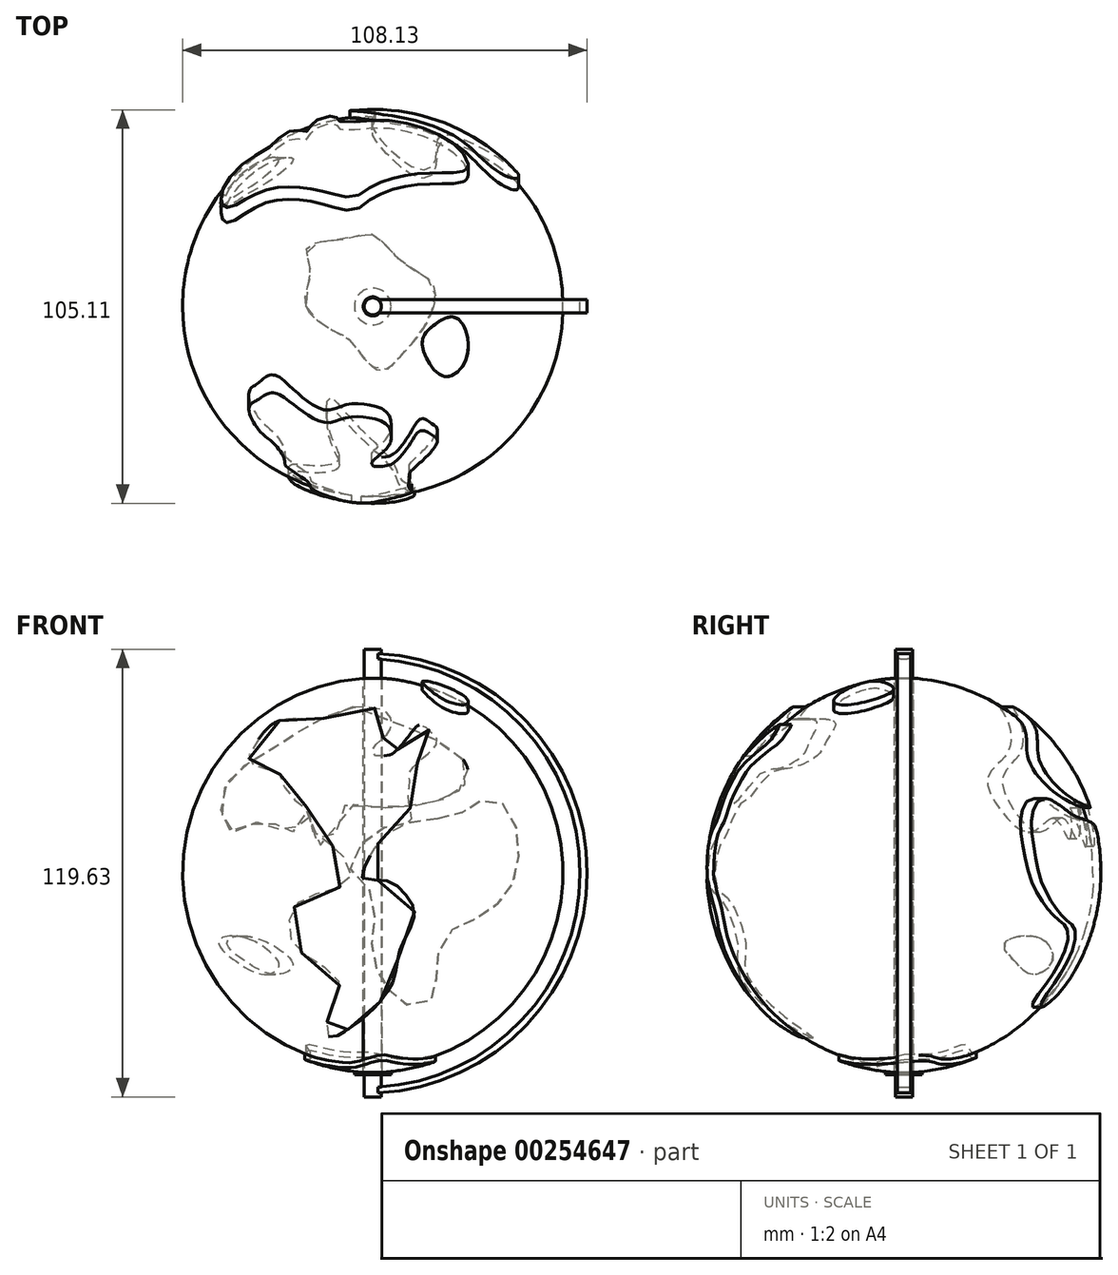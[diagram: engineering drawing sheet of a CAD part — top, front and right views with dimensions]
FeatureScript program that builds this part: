
annotation { "Feature Type Name" : "Feature", "Feature Type Description" : "" }
export const myFeature = defineFeature(function(context is Context, id is Id, definition is map)
    precondition{}
    {
        {
            var Q0;
            Q0=qCreatedBy(makeId("Front.planeOp"),FACE);
            var sketch = newSketch(context, id + "F0", { "sketchPlane" : qUnion([Q0])});
            skLineSegment(sketch, "E0", {"start": v(0, 76.2) * mm, "end": v(0, -76.2) * mm, "construction": true});
            skLineSegment(sketch, "E1", {"start": v(-76.2, 0) * mm, "end": v(76.2, 0) * mm, "construction": true});
            skLineSegment(sketch, "E2", {"start": v(0, 0) * mm, "end": v(0, 50.8) * mm});
            skLineSegment(sketch, "E3", {"start": v(0, 0) * mm, "end": v(0, -53.5) * mm});
            skLineSegment(sketch, "E4", {"start": v(0, 0) * mm, "end": v(50.8, 0) * mm});
            skArc(sketch, "E5", {"start": v(0, -53.5) * mm, "mid": v(50.82, -1.35) * mm, "end": v(0, 50.8) * mm});
            skSolve(sketch);
        }
        {
            var Q0;
            Q0 = qSketchRegion(id + "F0", true);
            var Q1;
            Q1=sQuery(id+"F0.wireOp",EDGE,"E0");
            revolve(context, id + "F1", {"entities" : qUnion([Q0]), "axis" : qUnion([Q1]), "revolveType" : RevolveType.FULL});
        }
        {
            var Q0;
            Q0=qCreatedBy(makeId("Front.planeOp"),FACE);
            var sketch = newSketch(context, id + "F2", { "sketchPlane" : qUnion([Q0])});
            skFitSpline(sketch, "E6", {"points": [v(24.15, 28.93) * mm, v(0, 41.12) * mm, v(-5.65, 42.93) * mm, v(-17.84, 37.5) * mm, v(-30.04, 29.83) * mm, v(-38.16, 23.96) * mm, v(-40.42, 14.93) * mm, v(-36.8, 9.52) * mm, v(-27.33, 13.13) * mm, v(-23.71, 7.71) * mm, v(-18.75, 14.48) * mm, v(-17.84, 15.84) * mm, v(-13.78, 5.9) * mm, v(-10.17, 8.61) * mm, v(-7.91, 16.29) * mm, v(0, 16.29) * mm, v(7.44, 16.29) * mm, v(22.8, 20.35) * mm, v(24.15, 28.93) * mm]});
            skFitSpline(sketch, "E7", {"points": [v(17.37, 13.13) * mm, v(24.15, 14.93) * mm, v(31.37, 18.55) * mm, v(37.7, 12.68) * mm, v(38.6, 0) * mm, v(35.88, -6.74) * mm, v(28.66, -13.06) * mm, v(20.98, -16.67) * mm, v(17.37, -23.44) * mm, v(16.02, -34.73) * mm, v(10.15, -36.99) * mm, v(0, -23.44) * mm, v(0, -7.19) * mm, v(-6.1, 0) * mm, v(0, 9.06) * mm, v(7.44, 11.77) * mm, v(17.37, 13.13) * mm]});
            skSolve(sketch);
        }
        {
            var Q0;
            Q0 = qSketchRegion(id + "F2", true);
            extrude(context, id + "F3", {"entities" : qUnion([Q0]), "operationType" : NewBodyOperationType.ADD, "oppositeDirection" : true, "depth" : 54.36 * mm, "hasSecondDirection" : true, "secondDirectionOppositeDirection" : true, "secondDirectionDepth" : 11.18 * mm});
        }
        {
            var Q0;
            Q0=qCreatedBy(makeId("Right.planeOp"),FACE);
            var sketch = newSketch(context, id + "F4", { "sketchPlane" : qUnion([Q0])});
            skFitSpline(sketch, "E8", {"points": [v(36.7, -18.93) * mm, v(39.41, -25.7) * mm, v(34, -28.41) * mm, v(29.93, -25.25) * mm, v(26.77, -20.28) * mm, v(36.7, -18.93) * mm]});
            skSolve(sketch);
        }
        {
            var Q0;
            Q0 = qSketchRegion(id + "F4", true);
            extrude(context, id + "F5", {"entities" : qUnion([Q0]), "operationType" : NewBodyOperationType.ADD, "oppositeDirection" : true, "depth" : 56.4 * mm, "hasSecondDirection" : true, "secondDirectionOppositeDirection" : true, "secondDirectionDepth" : 6.6 * mm});
        }
        {
            var Q0;
            Q0=qCreatedBy(makeId("Front.planeOp"),FACE);
            var sketch = newSketch(context, id + "F6", { "sketchPlane" : qUnion([Q0])});
            skArc(sketch, "E9", {"start": v(0, -54.77) * mm, "mid": v(52.65, -1.08) * mm, "end": v(0, 52.61) * mm});
            skLineSegment(sketch, "E10", {"start": v(0, 52.61) * mm, "end": v(0, 70.09) * mm});
            skLineSegment(sketch, "E11", {"start": v(0, 70.09) * mm, "end": v(87.72, 70.09) * mm});
            skLineSegment(sketch, "E12", {"start": v(87.72, 70.09) * mm, "end": v(87.72, -75.77) * mm});
            skLineSegment(sketch, "E13", {"start": v(87.72, -75.77) * mm, "end": v(0, -75.77) * mm});
            skLineSegment(sketch, "E14", {"start": v(0, -75.77) * mm, "end": v(0, -54.77) * mm});
            skSolve(sketch);
        }
        {
            var Q0;
            Q0 = qSketchRegion(id + "F2", true);
            extrude(context, id + "F7", {"entities" : qUnion([Q0]), "operationType" : NewBodyOperationType.ADD, "oppositeDirection" : true, "depth" : 57.66 * mm});
        }
        {
            var Q0;
            Q0=qCreatedBy(makeId("Front.planeOp"),FACE);
            var sketch = newSketch(context, id + "F8", { "sketchPlane" : qUnion([Q0])});
            skFitSpline(sketch, "E15", {"points": [v(-24.96, 39.32) * mm, v(-30.83, 33.9) * mm, v(-33.09, 29.38) * mm, v(-30.38, 26.67) * mm, v(-26.32, 26.22) * mm, v(-23.6, 22.61) * mm, v(-23.16, 19.45) * mm, v(-17.74, 16.29) * mm, v(-16.38, 10.42) * mm, v(-14.13, 8.16) * mm, v(-11.87, 6.8) * mm, v(-6, 0) * mm, v(-6.45, -3.58) * mm, v(-12.32, -6.29) * mm, v(-20.9, -10.35) * mm, v(-21.8, -19.38) * mm, v(-17.74, -23.44) * mm, v(-14.13, -25.7) * mm, v(-9.16, -30.22) * mm, v(-9.61, -34.28) * mm, v(-11.87, -39.7) * mm, v(-11.87, -45.12) * mm, v(-9.16, -44.66) * mm, v(0, -37.9) * mm, v(5.74, -29.31) * mm, v(7.55, -21.19) * mm, v(11.16, -11.7) * mm, v(7.55, -5.83) * mm, v(4.39, -3.58) * mm, v(-2.7, -2.7) * mm, v(-2.3, 0) * mm, v(3.67, 8.81) * mm, v(10.25, 12.93) * mm, v(9.64, 17.45) * mm, v(9.84, 23) * mm, v(9.84, 25.48) * mm, v(12.52, 28.56) * mm, v(17.25, 33.5) * mm, v(16.01, 35.76) * mm, v(12.93, 38.23) * mm, v(10.66, 36.58) * mm, v(5.73, 30.82) * mm, v(3.26, 30) * mm, v(0, 30.2) * mm, v(0, 31.85) * mm, v(3.26, 35.14) * mm, v(4.9, 37.82) * mm, v(4.29, 40.9) * mm, v(0, 42.76) * mm, v(-7.03, 42.34) * mm, v(-13.4, 39.88) * mm, v(-24.96, 39.32) * mm]});
            skSolve(sketch);
        }
        {
            var Q0;
            Q0 = qSketchRegion(id + "F8", true);
            extrude(context, id + "F9", {"entities" : qUnion([Q0]), "operationType" : NewBodyOperationType.ADD, "depth" : 55.37 * mm});
        }
        {
            var Q0;
            Q0=qCreatedBy(makeId("Top.planeOp"),FACE);
            var sketch = newSketch(context, id + "F10", { "sketchPlane" : qUnion([Q0])});
            skFitSpline(sketch, "E16", {"points": [v(-17.86, 0) * mm, v(-16.63, 9.09) * mm, v(-17.45, 15.87) * mm, v(-6.96, 18.14) * mm, v(0, 19.17) * mm, v(8.06, 11.76) * mm, v(16.29, 5.38) * mm, v(13.82, -5.32) * mm, v(6.62, -14.16) * mm, v(1.68, -17.25) * mm, v(-5.73, -9.43) * mm, v(-8.81, -7.37) * mm, v(-17.86, 0) * mm]});
            skSolve(sketch);
        }
        {
            var Q0;
            Q0 = qSketchRegion(id + "F10", true);
            extrude(context, id + "F11", {"entities" : qUnion([Q0]), "operationType" : NewBodyOperationType.ADD, "oppositeDirection" : true, "depth" : 64 * mm});
        }
        {
            var Q0;
            Q0=qCreatedBy(makeId("Top.planeOp"),FACE);
            var sketch = newSketch(context, id + "F12", { "sketchPlane" : qUnion([Q0])});
            skFitSpline(sketch, "E17", {"points": [v(13.2, -10.11) * mm, v(18.14, -18.34) * mm, v(22.87, -17.31) * mm, v(25.54, -10.32) * mm, v(22.05, -2.91) * mm, v(15.88, -5.38) * mm, v(13.2, -10.11) * mm]});
            skSolve(sketch);
        }
        {
            var Q0;
            Q0 = qSketchRegion(id + "F12", true);
            extrude(context, id + "F13", {"entities" : qUnion([Q0]), "operationType" : NewBodyOperationType.ADD, "depth" : 55.12 * mm});
        }
        {
            var Q0;
            Q0 = qSketchRegion(id + "F6", true);
            var Q1;
            Q1=sQuery(id+"F6.wireOp",EDGE,"E10");
            revolve(context, id + "F14", {"operationType" : NewBodyOperationType.REMOVE, "entities" : qUnion([Q0]), "axis" : qUnion([Q1]), "revolveType" : RevolveType.FULL, "oppositeDirection" : true});
        }
        {
            var Q0;
            Q0=qCreatedBy(makeId("Top.planeOp"),FACE);
            var sketch = newSketch(context, id + "F15", { "sketchPlane" : qUnion([Q0])});
            skCircle(sketch, "E18", {"center": v(0, 0) * mm, "radius": 2.54 * mm});
            skSolve(sketch);
        }
        {
            var Q0;
            Q0 = qSketchRegion(id + "F15", true);
            extrude(context, id + "F16", {"entities" : qUnion([Q0]), "operationType" : NewBodyOperationType.REMOVE, "oppositeDirection" : true, "depth" : 58.67 * mm, "hasSecondDirection" : true, "secondDirectionOppositeDirection" : false, "secondDirectionDepth" : 69.1 * mm});
        }
        {
            var Q0;
            Q0=qCreatedBy(makeId("Top.planeOp"),FACE);
            var sketch = newSketch(context, id + "F17", { "sketchPlane" : qUnion([Q0])});
            skCircle(sketch, "E19", {"center": v(0, 0) * mm, "radius": 2.29 * mm});
            skSolve(sketch);
        }
        {
            var Q0;
            Q0 = qSketchRegion(id + "F17", true);
            extrude(context, id + "F18", {"entities" : qUnion([Q0]), "depth" : 58.42 * mm, "hasSecondDirection" : true, "secondDirectionOppositeDirection" : true, "secondDirectionDepth" : 61.2 * mm});
        }
        {
            var Q0;
            Q0=qCreatedBy(makeId("Front.planeOp"),FACE);
            var sketch = newSketch(context, id + "F19", { "sketchPlane" : qUnion([Q0])});
            skPoint(sketch, "E20", {"position": v(0, -58.67) * mm});
            skPoint(sketch, "E21", {"position": v(0, 55.88) * mm});
            skArc(sketch, "E22", {"start": v(0, -58.67) * mm, "mid": v(55.4, -1.4) * mm, "end": v(0, 55.88) * mm});
            skArc(sketch, "E23", {"start": v(0, -60.18) * mm, "mid": v(57.3, -1.45) * mm, "end": v(0, 57.29) * mm});
            skLineSegment(sketch, "E24", {"start": v(0, 57.29) * mm, "end": v(0, 55.88) * mm});
            skLineSegment(sketch, "E25", {"start": v(0, -58.67) * mm, "end": v(0, -60.18) * mm});
            skSolve(sketch);
        }
        {
            var Q0;
            Q0=qCreatedBy(makeId("Front.planeOp"),FACE);
            var sketch = newSketch(context, id + "F20", { "sketchPlane" : qUnion([Q0])});
            skLineSegment(sketch, "E26", {"start": v(-4.89, -55.24) * mm, "end": v(0, -55.24) * mm});
            skLineSegment(sketch, "E27", {"start": v(0, -54.9) * mm, "end": v(-4.89, -54.9) * mm});
            skLineSegment(sketch, "E28", {"start": v(-4.89, -54.9) * mm, "end": v(-4.89, -55.24) * mm});
            skLineSegment(sketch, "E29", {"start": v(0, -55.24) * mm, "end": v(0, -54.9) * mm});
            skSolve(sketch);
        }
        {
            var Q0;
            Q0 = qSketchRegion(id + "F20", true);
            var Q1;
            Q1=sQuery(id+"F20.wireOp",EDGE,"E29");
            revolve(context, id + "F21", {"operationType" : NewBodyOperationType.ADD, "entities" : qUnion([Q0]), "axis" : qUnion([Q1]), "revolveType" : RevolveType.FULL});
        }
        {
            var Q0;
            Q0 = qSketchRegion(id + "F19", true);
            extrude(context, id + "F22", {"entities" : qUnion([Q0]), "operationType" : NewBodyOperationType.ADD, "depth" : 1.78 * mm, "hasSecondDirection" : true, "secondDirectionOppositeDirection" : true, "secondDirectionDepth" : 1.78 * mm});
        }
    });
